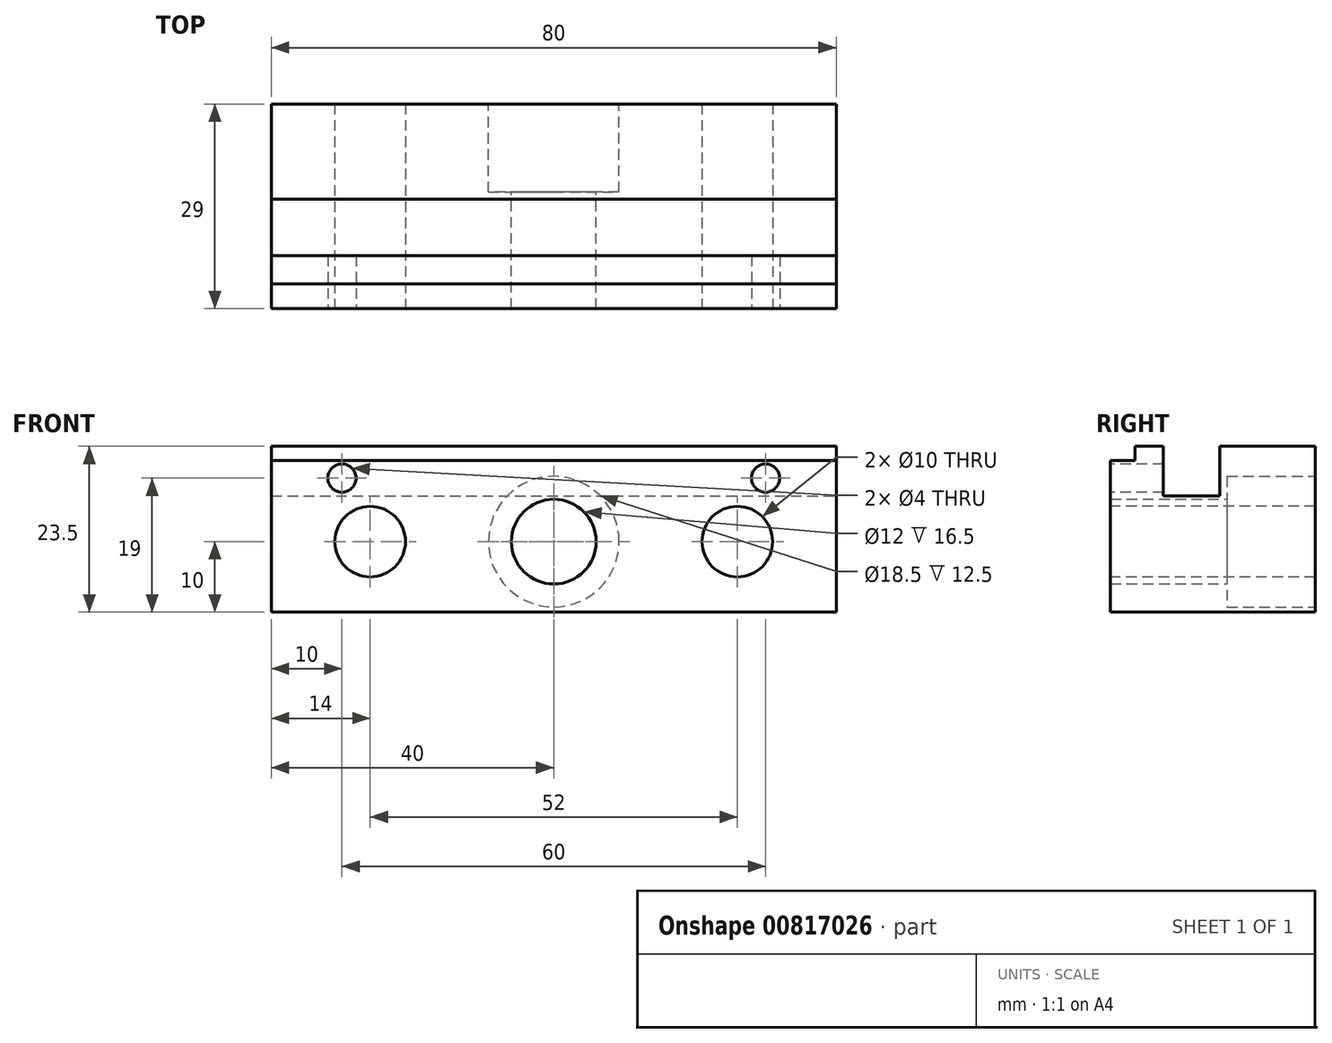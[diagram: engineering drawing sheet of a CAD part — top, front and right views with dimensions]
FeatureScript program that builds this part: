
annotation { "Feature Type Name" : "Feature", "Feature Type Description" : "" }
export const myFeature = defineFeature(function(context is Context, id is Id, definition is map)
    precondition{}
    {
        {
            var Q0;
            Q0=qCreatedBy(makeId("Front.planeOp"),FACE);
            var sketch = newSketch(context, id + "F0", { "sketchPlane" : qUnion([Q0])});
            skLineSegment(sketch, "E0.bottom", {"start": v(-40, 13.5) * mm, "end": v(40, 13.5) * mm});
            skLineSegment(sketch, "E0.top", {"start": v(-40, -10) * mm, "end": v(40, -10) * mm});
            skLineSegment(sketch, "E0.left", {"start": v(-40, 13.5) * mm, "end": v(-40, -10) * mm});
            skLineSegment(sketch, "E0.right", {"start": v(40, 13.5) * mm, "end": v(40, -10) * mm});
            skPoint(sketch, "E0.middle", {"position": v(0, 0) * mm});
            skSolve(sketch);
        }
        {
            var Q0;
            Q0 = qSketchRegion(id + "F0", true);
            extrude(context, id + "F1", {"entities" : qUnion([Q0]), "endBound" : BoundingType.SYMMETRIC, "depth" : 29 * mm, "offsetDistance" : 25 * mm});
        }
        {
            var Q0;
            Q0=makeQuery(id+"F1.opExtrude","CAP_FACE",FACE,{"disambiguationData":[OSD([sQuery(id+"F0.wireOp",EDGE,"E0.bottom"),sQuery(id+"F0.wireOp",EDGE,"E0.top"),sQuery(id+"F0.wireOp",EDGE,"E0.left"),sQuery(id+"F0.wireOp",EDGE,"E0.right")])],"isStart":false});
            var sketch = newSketch(context, id + "F2", { "sketchPlane" : qUnion([Q0])});
            skLineSegment(sketch, "E1.bottom", {"start": v(-40, 13.5) * mm, "end": v(40, 13.5) * mm});
            skLineSegment(sketch, "E1.top", {"start": v(-40, 11.5) * mm, "end": v(40, 11.5) * mm});
            skLineSegment(sketch, "E1.left", {"start": v(-40, 13.5) * mm, "end": v(-40, 11.5) * mm});
            skLineSegment(sketch, "E1.right", {"start": v(40, 13.5) * mm, "end": v(40, 11.5) * mm});
            skSolve(sketch);
        }
        {
            var Q0;
            Q0 = qSketchRegion(id + "F2", true);
            extrude(context, id + "F3", {"entities" : qUnion([Q0]), "operationType" : NewBodyOperationType.REMOVE, "oppositeDirection" : true, "depth" : 3.5 * mm, "offsetDistance" : 25 * mm});
        }
        {
            var Q0;
            Q0=makeQuery(id+"F1.opExtrude","CAP_FACE",FACE,{"disambiguationData":[OSD([sQuery(id+"F0.wireOp",EDGE,"E0.bottom"),sQuery(id+"F0.wireOp",EDGE,"E0.top"),sQuery(id+"F0.wireOp",EDGE,"E0.left"),sQuery(id+"F0.wireOp",EDGE,"E0.right")])],"isStart":true});
            var sketch = newSketch(context, id + "F4", { "sketchPlane" : qUnion([Q0])});
            skCircle(sketch, "E2", {"center": v(0, 0) * mm, "radius": 6 * mm});
            skSolve(sketch);
        }
        {
            var Q0;
            Q0 = qSketchRegion(id + "F4", true);
            extrude(context, id + "F5", {"entities" : qUnion([Q0]), "operationType" : NewBodyOperationType.REMOVE, "endBound" : BoundingType.THROUGH_ALL, "oppositeDirection" : true, "depth" : 12.5 * mm, "offsetDistance" : 25 * mm});
        }
        {
            var Q0;
            Q0=makeQuery(id+"F1.opExtrude","CAP_FACE",FACE,{"disambiguationData":[OSD([sQuery(id+"F0.wireOp",EDGE,"E0.bottom"),sQuery(id+"F0.wireOp",EDGE,"E0.top"),sQuery(id+"F0.wireOp",EDGE,"E0.left"),sQuery(id+"F0.wireOp",EDGE,"E0.right")])],"isStart":true});
            var sketch = newSketch(context, id + "F6", { "sketchPlane" : qUnion([Q0])});
            skCircle(sketch, "E3", {"center": v(0, 0) * mm, "radius": 9.25 * mm});
            skSolve(sketch);
        }
        {
            var Q0;
            Q0 = qSketchRegion(id + "F6", true);
            extrude(context, id + "F7", {"entities" : qUnion([Q0]), "operationType" : NewBodyOperationType.REMOVE, "oppositeDirection" : true, "depth" : 12.5 * mm, "offsetDistance" : 25 * mm});
        }
        {
            var Q0;
            Q0=makeQuery(id+"F1.opExtrude","CAP_FACE",FACE,{"disambiguationData":[OSD([sQuery(id+"F0.wireOp",EDGE,"E0.bottom"),sQuery(id+"F0.wireOp",EDGE,"E0.top"),sQuery(id+"F0.wireOp",EDGE,"E0.left"),sQuery(id+"F0.wireOp",EDGE,"E0.right")])],"isStart":false});
            var sketch = newSketch(context, id + "F8", { "sketchPlane" : qUnion([Q0])});
            skCircle(sketch, "E4", {"center": v(-26, 0) * mm, "radius": 5 * mm});
            skCircle(sketch, "E5.MirrorC", {"center": v(26, 0) * mm, "radius": 5 * mm});
            skSolve(sketch);
        }
        {
            var Q0;
            Q0 = qSketchRegion(id + "F8", true);
            extrude(context, id + "F9", {"entities" : qUnion([Q0]), "operationType" : NewBodyOperationType.REMOVE, "endBound" : BoundingType.THROUGH_ALL, "oppositeDirection" : true, "depth" : 25 * mm, "offsetDistance" : 25 * mm});
        }
        {
            var Q0;
            Q0=makeQuery(id+"F1.opExtrude","SWEPT_FACE",FACE,{"disambiguationData":[OSD([sQuery(id+"F0.wireOp",EDGE,"E0.bottom")])]});
            var sketch = newSketch(context, id + "F10", { "sketchPlane" : qUnion([Q0])});
            skLineSegment(sketch, "E6.bottom", {"start": v(-40, -7) * mm, "end": v(40, -7) * mm});
            skLineSegment(sketch, "E6.top", {"start": v(-40, 1) * mm, "end": v(40, 1) * mm});
            skLineSegment(sketch, "E6.left", {"start": v(-40, -7) * mm, "end": v(-40, 1) * mm});
            skLineSegment(sketch, "E6.right", {"start": v(40, -7) * mm, "end": v(40, 1) * mm});
            skSolve(sketch);
        }
        {
            var Q0;
            Q0 = qSketchRegion(id + "F10", true);
            extrude(context, id + "F11", {"entities" : qUnion([Q0]), "operationType" : NewBodyOperationType.REMOVE, "oppositeDirection" : true, "depth" : 7 * mm, "offsetDistance" : 25 * mm});
        }
        {
            var Q0;
            Q0=makeQuery(id+"F1.opExtrude","CAP_FACE",FACE,{"disambiguationData":[OSD([sQuery(id+"F0.wireOp",EDGE,"E0.bottom"),sQuery(id+"F0.wireOp",EDGE,"E0.top"),sQuery(id+"F0.wireOp",EDGE,"E0.left"),sQuery(id+"F0.wireOp",EDGE,"E0.right")])],"isStart":false});
            var sketch = newSketch(context, id + "F12", { "sketchPlane" : qUnion([Q0])});
            skCircle(sketch, "E7", {"center": v(-30, 9) * mm, "radius": 2 * mm});
            skCircle(sketch, "E8.MirrorC", {"center": v(30, 9) * mm, "radius": 2 * mm});
            skSolve(sketch);
        }
        {
            var Q0;
            Q0 = qSketchRegion(id + "F12", true);
            extrude(context, id + "F13", {"entities" : qUnion([Q0]), "operationType" : NewBodyOperationType.REMOVE, "oppositeDirection" : true, "depth" : 8 * mm, "offsetDistance" : 25 * mm});
        }
    });
